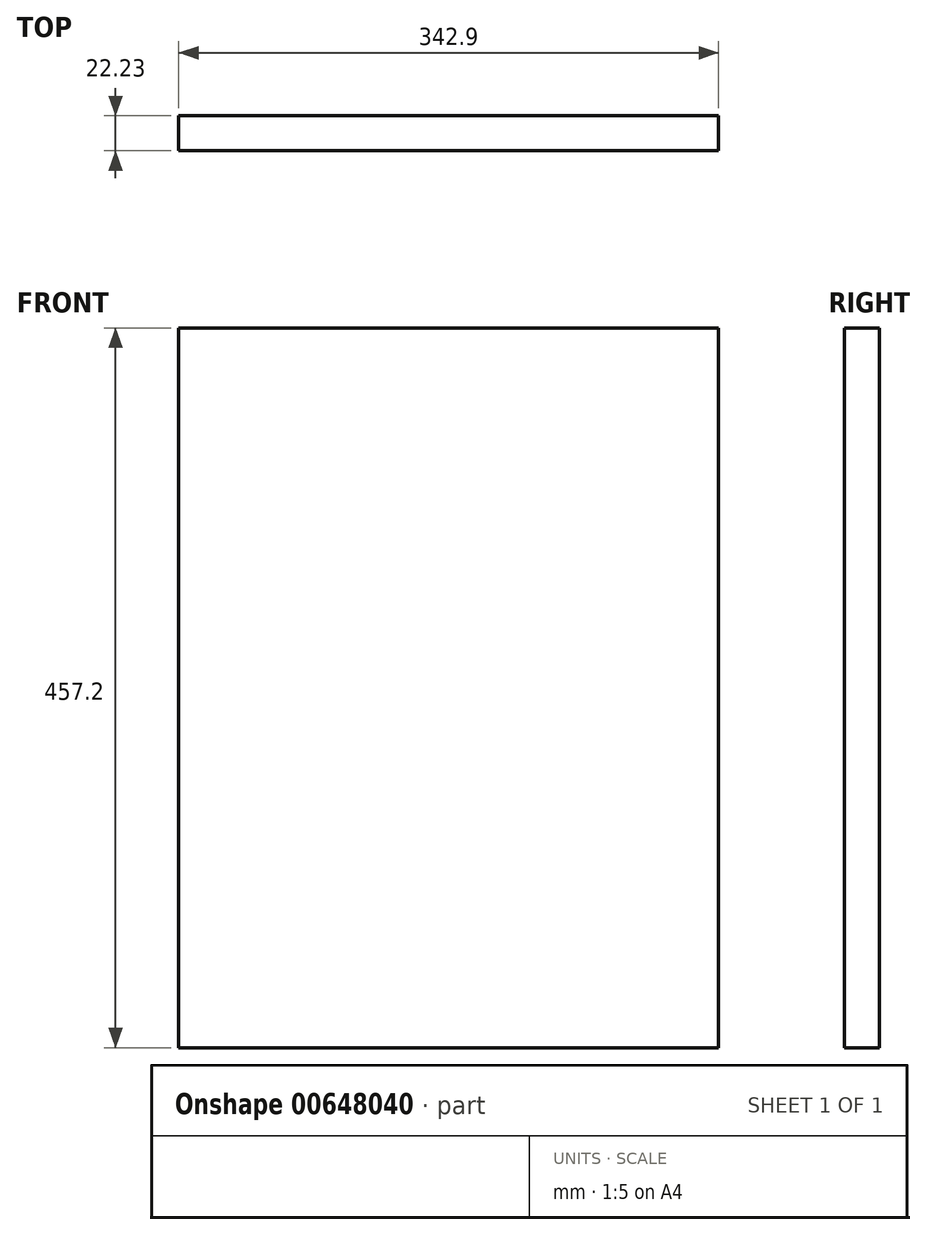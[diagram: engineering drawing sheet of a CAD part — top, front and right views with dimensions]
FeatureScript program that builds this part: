
annotation { "Feature Type Name" : "Feature", "Feature Type Description" : "" }
export const myFeature = defineFeature(function(context is Context, id is Id, definition is map)
    precondition{}
    {
        {
            var Q0;
            Q0=qCreatedBy(makeId("Front.planeOp"),FACE);
            var sketch = newSketch(context, id + "F0", { "sketchPlane" : qUnion([Q0])});
            skLineSegment(sketch, "E0.bottom", {"start": v(-171.45, 228.6) * mm, "end": v(171.45, 228.6) * mm});
            skLineSegment(sketch, "E0.top", {"start": v(-171.45, -228.6) * mm, "end": v(171.45, -228.6) * mm});
            skLineSegment(sketch, "E0.left", {"start": v(-171.45, 228.6) * mm, "end": v(-171.45, -228.6) * mm});
            skLineSegment(sketch, "E0.right", {"start": v(171.45, 228.6) * mm, "end": v(171.45, -228.6) * mm});
            skPoint(sketch, "E0.middle", {"position": v(0, 0) * mm});
            skSolve(sketch);
        }
        {
            var Q0;
            Q0=makeQuery(id+"F0.imprint","IMPRINT",FACE,{"disambiguationData":[TD([[makeQuery(id+"F0.imprint","IMPRINT",EDGE,{"derivedFrom":sQuery(id+"F0.wireOp",EDGE,"E0.bottom")}),-1.0]])]});
            extrude(context, id + "F1", {"entities" : qUnion([Q0]), "depth" : 22.22 * mm, "offsetDistance" : 25.4 * mm});
        }
    });
